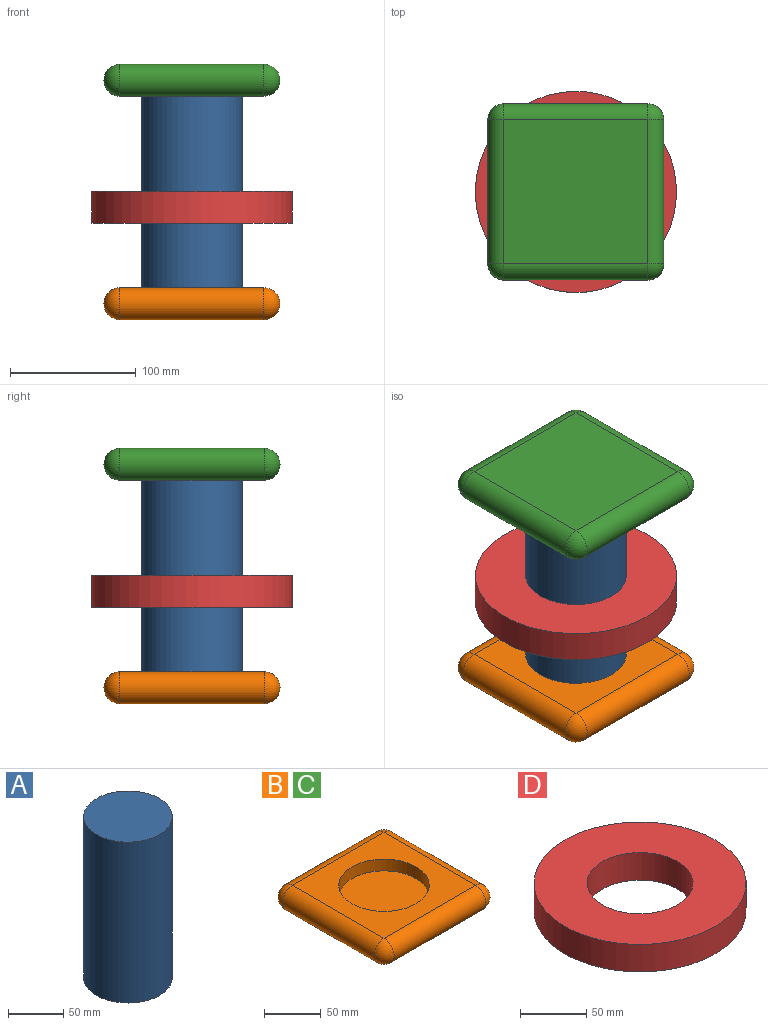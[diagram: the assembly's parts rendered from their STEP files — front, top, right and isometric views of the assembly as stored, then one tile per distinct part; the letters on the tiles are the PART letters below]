
ASSEMBLY  parts=4 mates=7
PART A: 3 faces, bbox 80x80x177.8 mm
  f0: cylinder r=40mm len=177.8mm, axis (0,0,-1), area 44686mm2, adj f1,f2
  f1: plane 80x80mm, normal (0,0,1), area 5026.5mm2, adj f0
  f2: plane 80x80mm, normal (0,0,-1), area 5026.5mm2, adj f0
PART B: 12 faces, bbox 140x140x25.4 mm
  f0: plane 114.6x114.6mm, normal (0,0,1), area 8106.6mm2, adj f2,f5,f6,f9,f10
  f1: plane 114.6x114.6mm, normal (0,0,-1), area 13133.2mm2, adj f5,f6,f9,f10
  f2: cylinder r=40mm len=80mm, axis (0,0,1), area 3191.9mm2, adj f0,f3
  f3: plane 80x80mm, normal (0,0,1), area 5026.5mm2, adj f2
  f4: sphere r=12.7mm, area 506.7mm2, adj f5,f6
  f5: cylinder r=12.7mm len=114.6mm, axis (0,-1,0), area 4572.3mm2, adj f0,f1,f4,f7
  f6: cylinder r=12.7mm len=114.6mm, axis (-1,0,0), area 4572.3mm2, adj f0,f1,f4,f8
  f7: sphere r=12.7mm, area 506.7mm2, adj f5,f9
  f8: sphere r=12.7mm, area 506.7mm2, adj f6,f10
  f9: cylinder r=12.7mm len=114.6mm, axis (1,0,0), area 4572.3mm2, adj f0,f1,f7,f11
  f10: cylinder r=12.7mm len=114.6mm, axis (0,1,0), area 4572.3mm2, adj f0,f1,f8,f11
  f11: sphere r=12.7mm, area 506.7mm2, adj f9,f10
PART C: same geometry as B
PART D: 4 faces, bbox 160x160x25.4 mm
  f0: cylinder r=40mm len=80mm, axis (0,0,-1), area 6383.7mm2, adj f2,f3
  f1: cylinder r=80mm len=160mm, axis (0,0,-1), area 12767.4mm2, adj f2,f3
  f2: plane 160x160mm, normal (0,0,1), area 15079.6mm2, adj f0,f1
  f3: plane 160x160mm, normal (0,0,-1), area 15079.6mm2, adj f0,f1
PLACE A t=(68.39,-173.76,-0.06)mm
PLACE B t=(-0.24,-0.18,-12.76)mm fixed
PLACE C rot(axis=(1,0,0),180deg) t=(-0.24,-0.18,190.44)mm
PLACE D rot(axis=(1,0,0),180deg) t=(-94.14,211.27,89.3)mm
MATE slider D.f0 <-> A.f0  axis (0,0,1) through (-0.24,-0.18,76.6)mm
MATE planar A.f0 <-> B.f2  axis (0,0,-1) through (-0.24,-0.18,-0.06)mm
MATE parallel B.f0 <-> D.f0  axis (0,0,1) through (-57.54,-0.18,12.64)mm
MATE parallel D.f0 <-> C.f0  axis (0,0,1) through (-0.24,-0.18,89.3)mm
MATE fastened C.f2 <-> A.f0  axis (0,0,-1) through (-0.24,-0.18,177.74)mm
MATE fastened A.f0 <-> B.f2  axis (0,0,-1) through (-0.24,-0.18,-0.06)mm
MATE planar A.f0 <-> C.f2  axis (0,0,1) through (-0.24,-0.18,177.74)mm
